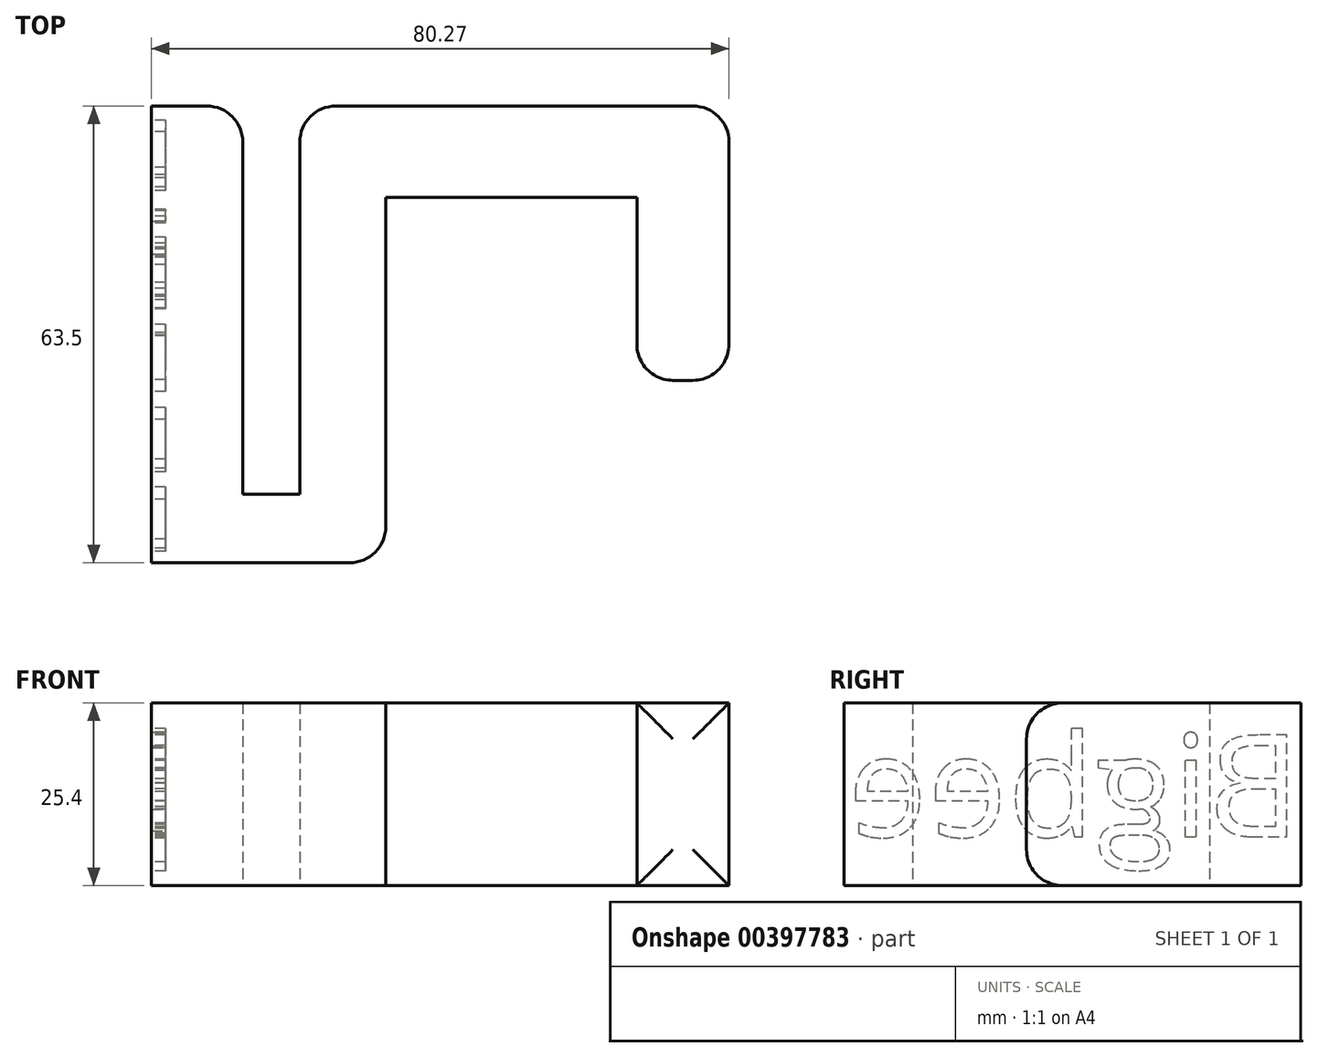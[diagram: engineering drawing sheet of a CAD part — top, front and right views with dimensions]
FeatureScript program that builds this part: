
annotation { "Feature Type Name" : "Feature", "Feature Type Description" : "" }
export const myFeature = defineFeature(function(context is Context, id is Id, definition is map)
    precondition{}
    {
        {
            var Q0;
            Q0=qCreatedBy(makeId("Top.planeOp"),FACE);
            var sketch = newSketch(context, id + "F0", { "sketchPlane" : qUnion([Q0])});
            skLineSegment(sketch, "E0", {"start": v(0, 0) * mm, "end": v(0, 63.5) * mm});
            skLineSegment(sketch, "E1", {"start": v(0, 63.5) * mm, "end": v(12.7, 63.5) * mm});
            skLineSegment(sketch, "E2", {"start": v(12.7, 63.5) * mm, "end": v(12.7, 9.53) * mm});
            skLineSegment(sketch, "E3", {"start": v(12.7, 9.53) * mm, "end": v(20.64, 9.53) * mm});
            skLineSegment(sketch, "E4", {"start": v(20.64, 9.53) * mm, "end": v(20.64, 63.5) * mm});
            skLineSegment(sketch, "E5", {"start": v(20.64, 63.5) * mm, "end": v(80.27, 63.5) * mm});
            skLineSegment(sketch, "E6", {"start": v(80.27, 63.5) * mm, "end": v(80.27, 25.35) * mm});
            skLineSegment(sketch, "E7", {"start": v(80.27, 25.35) * mm, "end": v(67.48, 25.35) * mm});
            skLineSegment(sketch, "E8", {"start": v(67.48, 25.35) * mm, "end": v(67.48, 50.8) * mm});
            skLineSegment(sketch, "E9", {"start": v(67.48, 50.8) * mm, "end": v(32.58, 50.8) * mm});
            skLineSegment(sketch, "E10", {"start": v(32.58, 50.8) * mm, "end": v(32.58, 0) * mm});
            skLineSegment(sketch, "E11", {"start": v(32.58, 0) * mm, "end": v(0, 0) * mm});
            skSolve(sketch);
        }
        {
            var Q0;
            Q0=makeQuery(id+"F0.imprint","IMPRINT",FACE,{"disambiguationData":[TD([[makeQuery(id+"F0.imprint","IMPRINT",EDGE,{"derivedFrom":sQuery(id+"F0.wireOp",EDGE,"E0")}),-1.0]])]});
            extrude(context, id + "F1", {"entities" : qUnion([Q0]), "depth" : 25.4 * mm});
        }
        {
            var Q0;
            Q0=makeQuery(id+"F1.opExtrude","SWEPT_FACE",FACE,{"disambiguationData":[OSD([sQuery(id+"F0.wireOp",EDGE,"E0")])]});
            var sketch = newSketch(context, id + "F2", { "sketchPlane" : qUnion([Q0])});
            skText(sketch, "E12", { "text": "Bigbee", "fontName": "OpenSans-Regular.ttf"});
            const initialGuessF2  = {"E12": [-0.0635, 0.00681, 1, 0, 0.01424]};
            skSetInitialGuess(sketch, initialGuessF2);
            skSolve(sketch);
        }
        {
            var Q0;
            Q0=qSketchRegion(id+"F2",true);
            extrude(context, id + "F3", {"entities" : qUnion([Q0]), "operationType" : NewBodyOperationType.REMOVE, "oppositeDirection" : true, "depth" : 2 * mm});
        }
        {
            var Q0;
            Q0=makeQuery(id+"F1.opExtrude","CAP_EDGE",EDGE,{"disambiguationData":[OSD([sQuery(id+"F0.wireOp",EDGE,"E7")])],"isStart":false});
            var Q1;
            Q1=makeQuery(id+"F1.opExtrude","CAP_EDGE",EDGE,{"disambiguationData":[OSD([sQuery(id+"F0.wireOp",EDGE,"E7")])],"isStart":true});
            var Q2;
            Q2=makeQuery(id+"F1.opExtrude","SWEPT_EDGE",EDGE,{"disambiguationData":[OSD([sQuery(id+"F0.wireOp",EDGE,"E6"),sQuery(id+"F0.wireOp",EDGE,"E7")])]});
            var Q3;
            Q3=makeQuery(id+"F1.opExtrude","SWEPT_EDGE",EDGE,{"disambiguationData":[OSD([sQuery(id+"F0.wireOp",EDGE,"E7"),sQuery(id+"F0.wireOp",EDGE,"E8")])]});
            var Q4;
            Q4=makeQuery(id+"F1.opExtrude","SWEPT_EDGE",EDGE,{"disambiguationData":[OSD([sQuery(id+"F0.wireOp",EDGE,"E5"),sQuery(id+"F0.wireOp",EDGE,"E6")])]});
            var Q5;
            Q5=makeQuery(id+"F1.opExtrude","SWEPT_EDGE",EDGE,{"disambiguationData":[OSD([sQuery(id+"F0.wireOp",EDGE,"E10"),sQuery(id+"F0.wireOp",EDGE,"E11")])]});
            var Q6;
            Q6=makeQuery(id+"F1.opExtrude","SWEPT_EDGE",EDGE,{"disambiguationData":[OSD([sQuery(id+"F0.wireOp",EDGE,"E4"),sQuery(id+"F0.wireOp",EDGE,"E5")])]});
            var Q7;
            Q7=makeQuery(id+"F1.opExtrude","SWEPT_EDGE",EDGE,{"disambiguationData":[OSD([sQuery(id+"F0.wireOp",EDGE,"E1"),sQuery(id+"F0.wireOp",EDGE,"E2")])]});
            fillet(context, id + "F4", {"entities" : qUnion([Q0, Q1, Q2, Q3, Q4, Q5, Q6, Q7]), "radius" : 5 * mm, "tangentPropagation" : true, "allowEdgeOverflow" : false});
        }
    });
